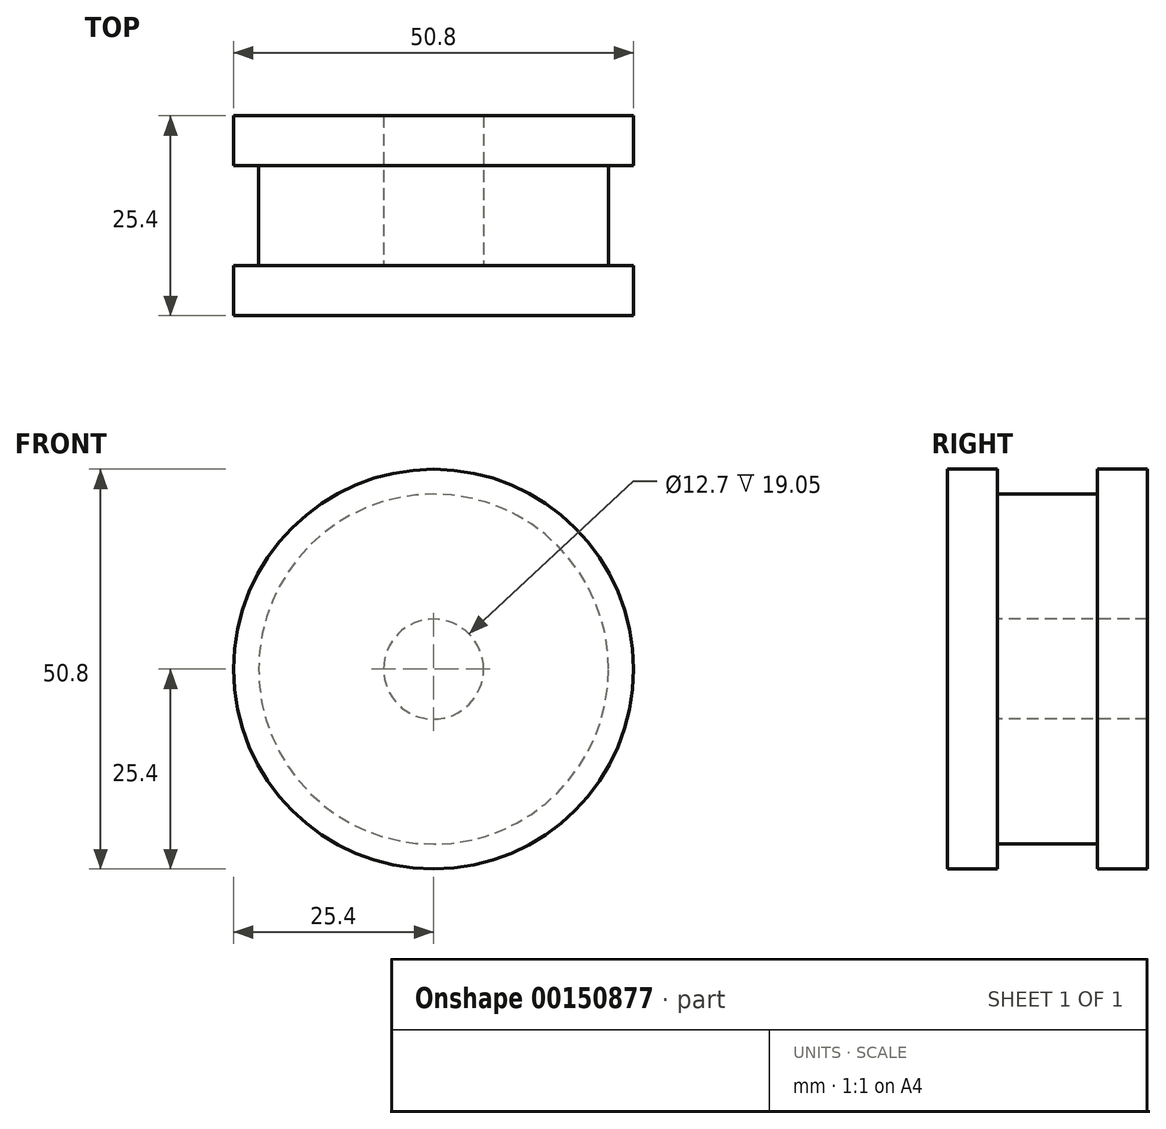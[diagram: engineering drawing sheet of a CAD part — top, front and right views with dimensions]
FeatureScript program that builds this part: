
annotation { "Feature Type Name" : "Feature", "Feature Type Description" : "" }
export const myFeature = defineFeature(function(context is Context, id is Id, definition is map)
    precondition{}
    {
        {
            var Q0;
            Q0=qCreatedBy(makeId("Front.planeOp"),FACE);
            var sketch = newSketch(context, id + "F0", { "sketchPlane" : qUnion([Q0])});
            skCircle(sketch, "E0", {"center": v(0, 0) * mm, "radius": 25.4 * mm});
            skSolve(sketch);
        }
        {
            var Q0;
            Q0 = qSketchRegion(id + "F0", true);
            extrude(context, id + "F1", {"entities" : qUnion([Q0]), "depth" : 6.35 * mm});
        }
        {
            var Q0;
            Q0=makeQuery(id+"F1.opExtrude","CAP_FACE",FACE,{"disambiguationData":[OSD([sQuery(id+"F0.wireOp",EDGE,"E0")])],"isStart":false});
            var sketch = newSketch(context, id + "F2", { "sketchPlane" : qUnion([Q0])});
            skCircle(sketch, "E1", {"center": v(0, 0) * mm, "radius": 22.23 * mm});
            skSolve(sketch);
        }
        {
            var Q0;
            Q0 = qSketchRegion(id + "F2", true);
            extrude(context, id + "F3", {"entities" : qUnion([Q0]), "operationType" : NewBodyOperationType.ADD, "depth" : 12.7 * mm});
        }
        {
            var Q0;
            Q0=makeQuery(id+"F3.opExtrude","CAP_FACE",FACE,{"disambiguationData":[OSD([sQuery(id+"F2.wireOp",EDGE,"E1")])],"isStart":false});
            var sketch = newSketch(context, id + "F4", { "sketchPlane" : qUnion([Q0])});
            skCircle(sketch, "E2", {"center": v(0, 0) * mm, "radius": 6.35 * mm});
            skSolve(sketch);
        }
        {
            var Q0;
            Q0 = qSketchRegion(id + "F4", true);
            extrude(context, id + "F5", {"entities" : qUnion([Q0]), "operationType" : NewBodyOperationType.REMOVE, "endBound" : BoundingType.THROUGH_ALL, "oppositeDirection" : true, "depth" : 12.7 * mm});
        }
        {
            var Q0;
            Q0=makeQuery(id+"F3.opExtrude","CAP_FACE",FACE,{"disambiguationData":[OSD([sQuery(id+"F2.wireOp",EDGE,"E1")])],"isStart":false});
            var sketch = newSketch(context, id + "F6", { "sketchPlane" : qUnion([Q0])});
            skCircle(sketch, "E3", {"center": v(0, 0) * mm, "radius": 25.4 * mm});
            skSolve(sketch);
        }
        {
            var Q0;
            Q0 = qSketchRegion(id + "F6", true);
            extrude(context, id + "F7", {"entities" : qUnion([Q0]), "operationType" : NewBodyOperationType.ADD, "depth" : 6.35 * mm});
        }
    });
